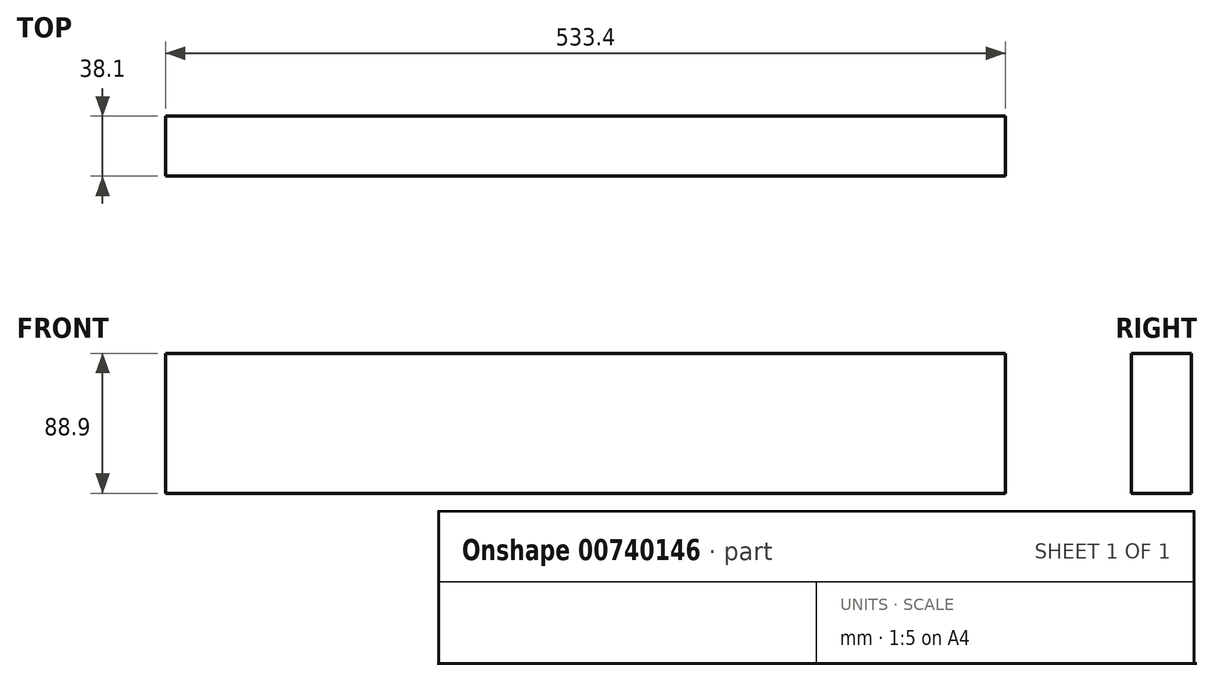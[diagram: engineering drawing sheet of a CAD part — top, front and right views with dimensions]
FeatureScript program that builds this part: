
annotation { "Feature Type Name" : "Feature", "Feature Type Description" : "" }
export const myFeature = defineFeature(function(context is Context, id is Id, definition is map)
    precondition{}
    {
        {
            var Q0;
            Q0=qCreatedBy(makeId("Right.planeOp"),FACE);
            var sketch = newSketch(context, id + "F0", { "sketchPlane" : qUnion([Q0])});
            skLineSegment(sketch, "E0.bottom", {"start": v(-79.68, 85.36) * mm, "end": v(-41.58, 85.36) * mm});
            skLineSegment(sketch, "E0.top", {"start": v(-79.68, -3.54) * mm, "end": v(-41.58, -3.54) * mm});
            skLineSegment(sketch, "E0.left", {"start": v(-79.68, 85.36) * mm, "end": v(-79.68, -3.54) * mm});
            skLineSegment(sketch, "E0.right", {"start": v(-41.58, 85.36) * mm, "end": v(-41.58, -3.54) * mm});
            skSolve(sketch);
        }
        {
            var Q0;
            Q0=makeQuery(id+"F0.imprint","IMPRINT",FACE,{"disambiguationData":[TD([[makeQuery(id+"F0.imprint","IMPRINT",EDGE,{"derivedFrom":sQuery(id+"F0.wireOp",EDGE,"E0.bottom")}),-1.0]])]});
            extrude(context, id + "F1", {"entities" : qUnion([Q0]), "depth" : 533.4 * mm, "offsetDistance" : 25.4 * mm});
        }
    });
